# Revit family: 306_ed62fd43d02542bbae0ffccc3da60c
name_source: partatom
category: Pipe Accessories
units: mm (PartAtom-declared; Revit-internal decimal feet)

## family parameters
Always vertical = Yes
Cut with Voids When Loaded = No
Part Type = Valve - Breaks Into
Round Connector Dimension = Use Diameter
Shared = No
Work Plane-Based = No

## types (4) — shared parameters
Description = 2-way Control valve with pressure balanced plug VLC225, PN25 flange
L2D_Min = 3048 mm
Manufacturer = ESBE
QmdConnectorList = 301;D;302;D
R9 = 4 mm  [stored 0.0131234 ft]
URL = http://www.esbe.eu
X1 = 2 mm  [stored 0.00656168 ft]
Z10 = 3 mm  [stored 0.00984252 ft]
Z14 = 2 mm  [stored 0.00656168 ft]
Z14__ve = -2 mm  [stored -0.00656168 ft]
Z4 = 14 mm  [stored 0.0459318 ft]
Z5 = 7 mm  [stored 0.0229659 ft]
Z6 = 10 mm  [stored 0.0328084 ft]
Z7 = 3 mm  [stored 0.00984252 ft]
Z8 = 15 mm  [stored 0.0492126 ft]
Z9 = 7 mm  [stored 0.0229659 ft]
magiPartTypeId = 306
magiProductFamilyId = ed62fd43d02542bbae0ffccc3da60c

## per-type parameters (varying)
- VLC225 PN25 FLANGE DN25-10: B1=117 mm; CenSd_R6_6=14 mm  [stored 0.0459318 ft]; D=25 mm; D2=39 mm; D3=36 mm; D4=30 mm  [stored 0.0984252 ft]; FDT2=58 mm; H3=45 mm; H4=96 mm; HCDT2=32 mm  [stored 0.104987 ft]; L2D=160 mm; LT2=80 mm; R1=19 mm; R3=29 mm; R4=23 mm; R5=19 mm; R6=16 mm; R7=9 mm  [stored 0.0295276 ft]; R8=7 mm  [stored 0.0229659 ft]; RD=33 mm; W2D=25 mm  [stored 0.082021 ft]; X2=12 mm  [stored 0.0393701 ft]; X2__ve=-12 mm; Z12=31 mm; Z12__ve=-31 mm; Z13=5 mm  [stored 0.0164042 ft]; Z15=16 mm; Z3=96 mm; magiProductId=0bba63fb31934fd5b8f69f1c51bffd
- VLC225 PN25 FLANGE DN50-38: B1=170 mm; CenSd_R6_6=20 mm  [stored 0.0656168 ft]; D=50 mm; D2=57 mm; D3=53 mm; D4=45 mm; FDT2=83 mm; H3=75 mm; H4=111 mm; HCDT2=48 mm; L2D=230 mm; LT2=115 mm; R1=29 mm; R3=42 mm; R4=34 mm; R5=27 mm; R6=23 mm; R7=14 mm  [stored 0.0459318 ft]; R8=10 mm  [stored 0.0328084 ft]; RD=48 mm; W2D=50 mm; X2=18 mm; X2__ve=-18 mm; Z12=45 mm; Z12__ve=-45 mm; Z13=6 mm  [stored 0.019685 ft]; Z15=26 mm; Z3=126 mm; magiProductId=75d7d9e62acb4504bc9bc277433001
- VLC225 PN25 FLANGE DN40-25: B1=147 mm; CenSd_R6_6=17 mm; D=40 mm; D2=49 mm; D3=46 mm; D4=39 mm; FDT2=75 mm; H3=60 mm; H4=99 mm; HCDT2=41 mm; L2D=200 mm; LT2=100 mm; R1=24 mm; R3=37 mm; R4=29 mm; R5=24 mm; R6=20 mm  [stored 0.0656168 ft]; R7=12 mm  [stored 0.0393701 ft]; R8=9 mm  [stored 0.0295276 ft]; RD=42 mm; W2D=40 mm; X2=16 mm; X2__ve=-16 mm  [stored -0.0524934 ft]; Z12=39 mm; Z12__ve=-39 mm  [stored -0.127953 ft]; Z13=5 mm  [stored 0.0164042 ft]; Z15=21 mm; Z3=106 mm; magiProductId=90eabcc0afc745af991fa0d23a6d83
- VLC225 PN25 FLANGE DN32-16: B1=132 mm; CenSd_R6_6=15 mm  [stored 0.0492126 ft]; D=32 mm; D2=44 mm; D3=41 mm; D4=34 mm; FDT2=70 mm; H3=58 mm; H4=100 mm; HCDT2=36 mm; L2D=180 mm; LT2=90 mm; R1=21 mm; R3=33 mm; R4=26 mm; R5=21 mm; R6=18 mm; R7=11 mm; R8=8 mm  [stored 0.0262467 ft]; RD=37 mm; W2D=32 mm  [stored 0.104987 ft]; X2=14 mm  [stored 0.0459318 ft]; X2__ve=-14 mm; Z12=35 mm; Z12__ve=-35 mm; Z13=5 mm  [stored 0.0164042 ft]; Z15=20 mm  [stored 0.0656168 ft]; Z3=109 mm; magiProductId=d21397777c5c44d293b8d1ddbf6d92

note: column(s) folded — value = type name in every type: magiProductCode

note: [stored X ft] marks values corroborated as IEEE doubles in the binary element streams (Revit-internal decimal feet)

## geometry (parser evidence)
native form markers: Sweep x3
no freeform markers — native parametric forms only
